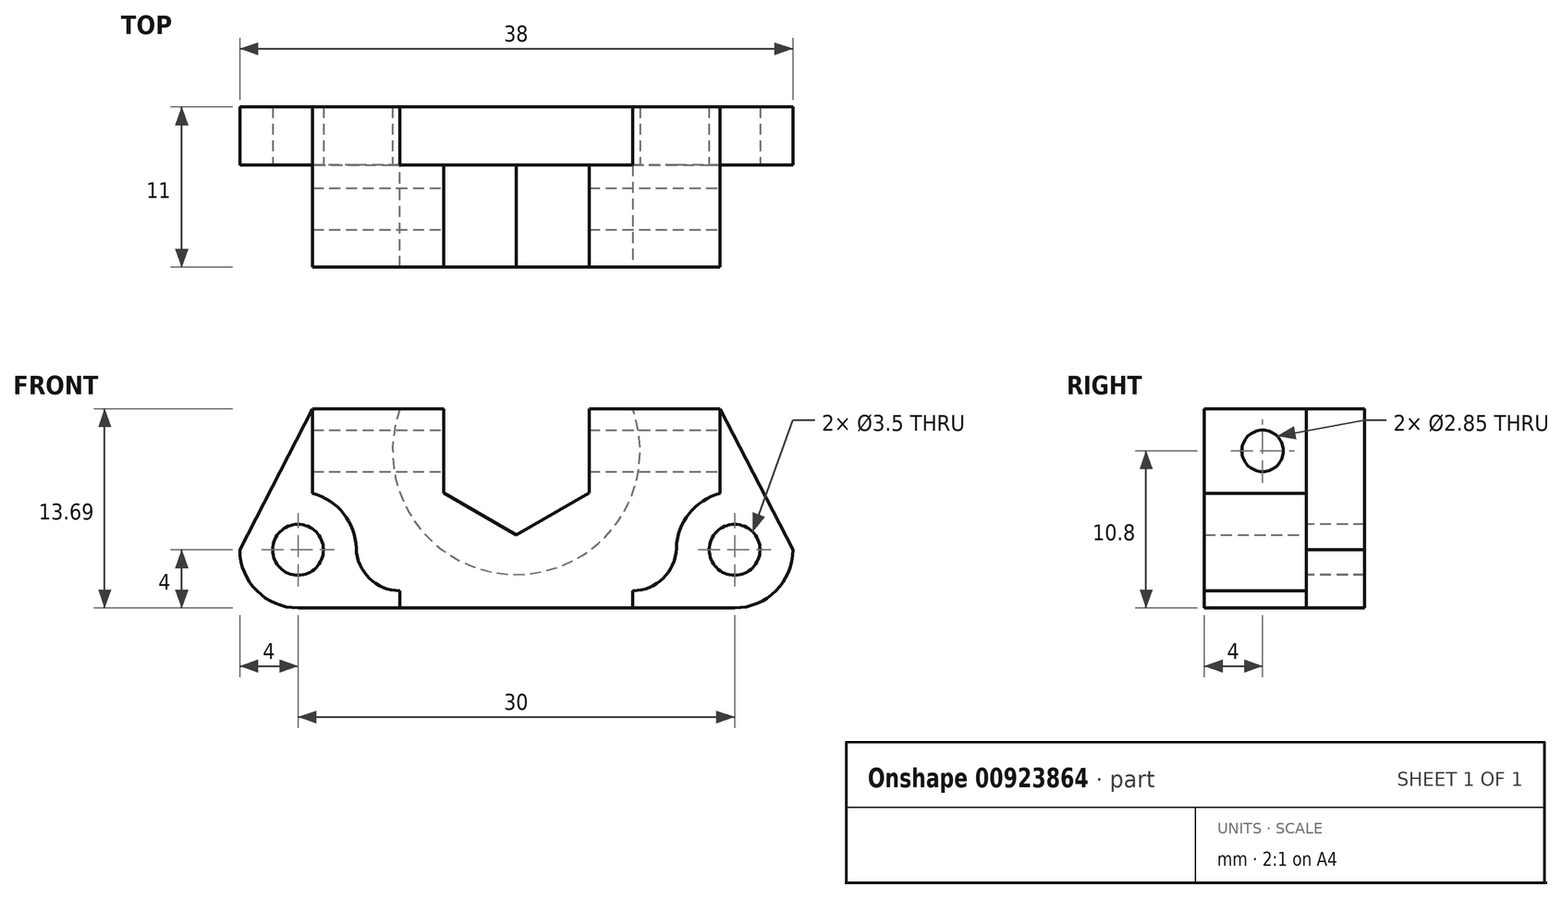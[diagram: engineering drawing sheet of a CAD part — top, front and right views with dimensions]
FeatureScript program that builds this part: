
annotation { "Feature Type Name" : "Feature", "Feature Type Description" : "" }
export const myFeature = defineFeature(function(context is Context, id is Id, definition is map)
    precondition{}
    {
        {
            var Q0;
            Q0=qCreatedBy(makeId("Front.planeOp"),FACE);
            var sketch = newSketch(context, id + "F0", { "sketchPlane" : qUnion([Q0])});
            skLineSegment(sketch, "E0.0", {"start": v(5, 2.89) * mm, "end": v(5, -2.89) * mm});
            skLineSegment(sketch, "E0.1", {"start": v(5, -2.89) * mm, "end": v(0, -5.77) * mm});
            skLineSegment(sketch, "E0.2", {"start": v(0, -5.77) * mm, "end": v(-5, -2.89) * mm});
            skLineSegment(sketch, "E0.3", {"start": v(-5, -2.89) * mm, "end": v(-5, 2.89) * mm});
            skPoint(sketch, "E0.0.midPoint", {"position": v(5, 0) * mm});
            skLineSegment(sketch, "E1", {"start": v(5, 2.89) * mm, "end": v(14, 2.89) * mm});
            skLineSegment(sketch, "E2", {"start": v(-5, 2.89) * mm, "end": v(-14, 2.89) * mm});
            skLineSegment(sketch, "E3.bottom", {"start": v(-14, 2.89) * mm, "end": v(-5, 2.89) * mm});
            skLineSegment(sketch, "E3.top", {"start": v(-14, -9.61) * mm, "end": v(14, -9.61) * mm});
            skLineSegment(sketch, "E3.left", {"start": v(-14, 2.89) * mm, "end": v(-14, -9.61) * mm});
            skLineSegment(sketch, "E3.right", {"start": v(14, 2.89) * mm, "end": v(14, -9.61) * mm});
            skSolve(sketch);
        }
        {
            var Q0;
            Q0 = qSketchRegion(id + "F0", true);
            extrude(context, id + "F1", {"entities" : qUnion([Q0]), "depth" : 7 * mm, "offsetDistance" : 25 * mm});
        }
        {
            var Q0;
            Q0=makeQuery(id+"F1.opExtrude","SWEPT_FACE",FACE,{"disambiguationData":[OSD([sQuery(id+"F0.wireOp",EDGE,"E3.right")])]});
            var sketch = newSketch(context, id + "F2", { "sketchPlane" : qUnion([Q0])});
            skLineSegment(sketch, "E4", {"start": v(0, 0) * mm, "end": v(-6, 0) * mm});
            skCircle(sketch, "E5", {"center": v(-3, 0) * mm, "radius": 1.43 * mm});
            skSolve(sketch);
        }
        {
            var Q0;
            Q0 = qSketchRegion(id + "F2", true);
            extrude(context, id + "F3", {"entities" : qUnion([Q0]), "operationType" : NewBodyOperationType.REMOVE, "oppositeDirection" : true, "depth" : 34.2 * mm, "offsetDistance" : 25 * mm});
        }
        {
            var Q0;
            Q0=makeQuery(id+"F1.opExtrude","CAP_FACE",FACE,{"disambiguationData":[OSD([sQuery(id+"F0.wireOp",EDGE,"E0.0"),sQuery(id+"F0.wireOp",EDGE,"E0.1"),sQuery(id+"F0.wireOp",EDGE,"E0.2"),sQuery(id+"F0.wireOp",EDGE,"E0.3"),sQuery(id+"F0.wireOp",EDGE,"E1"),sQuery(id+"F0.wireOp",EDGE,"E2"),sQuery(id+"F0.wireOp",EDGE,"E3.top"),sQuery(id+"F0.wireOp",EDGE,"E3.left"),sQuery(id+"F0.wireOp",EDGE,"E3.right")])],"isStart":true});
            var sketch = newSketch(context, id + "F4", { "sketchPlane" : qUnion([Q0])});
            skArc(sketch, "E6", {"start": v(-8, 2.89) * mm, "mid": v(0, -8.5) * mm, "end": v(8, 2.89) * mm});
            skLineSegment(sketch, "E7", {"start": v(0, 0) * mm, "end": v(0, -6.8) * mm});
            skLineSegment(sketch, "E8", {"start": v(0, -6.8) * mm, "end": v(-15, -6.8) * mm});
            skCircle(sketch, "E9", {"center": v(-15, -6.8) * mm, "radius": 1.75 * mm});
            skCircle(sketch, "E10.MirrorC", {"center": v(15, -6.8) * mm, "radius": 1.75 * mm});
            skLineSegment(sketch, "E11.0", {"start": v(8, 2.89) * mm, "end": v(14, 2.89) * mm});
            skLineSegment(sketch, "E12.0", {"start": v(-8, 2.89) * mm, "end": v(-14, 2.89) * mm});
            skArc(sketch, "E13", {"start": v(-19, -6.8) * mm, "mid": v(-17.83, -9.63) * mm, "end": v(-15, -10.8) * mm});
            skArc(sketch, "E14", {"start": v(15, -10.8) * mm, "mid": v(17.83, -9.63) * mm, "end": v(19, -6.8) * mm});
            skLineSegment(sketch, "E15", {"start": v(-14, 2.89) * mm, "end": v(-19, -6.8) * mm});
            skLineSegment(sketch, "E16.MirrorCS", {"start": v(14, 2.89) * mm, "end": v(19, -6.8) * mm});
            skLineSegment(sketch, "E17", {"start": v(15, -10.8) * mm, "end": v(-15, -10.8) * mm});
            skPoint(sketch, "E18.orphan", {"position": v(5, 2.89) * mm});
            skPoint(sketch, "E19.orphan", {"position": v(-5, 2.89) * mm});
            skSolve(sketch);
        }
        {
            var Q0;
            Q0 = qSketchRegion(id + "F4", true);
            extrude(context, id + "F5", {"entities" : qUnion([Q0]), "operationType" : NewBodyOperationType.ADD, "depth" : 4 * mm, "offsetDistance" : 25 * mm});
        }
        {
            var Q0;
            Q0=makeQuery(id+"F5.opExtrude","CAP_FACE",FACE,{"disambiguationData":[OSD([sQuery(id+"F4.wireOp",EDGE,"E6"),sQuery(id+"F4.wireOp",EDGE,"E9"),sQuery(id+"F4.wireOp",EDGE,"E10.MirrorC"),sQuery(id+"F4.wireOp",EDGE,"E11.0"),sQuery(id+"F4.wireOp",EDGE,"E12.0"),sQuery(id+"F4.wireOp",EDGE,"E13"),sQuery(id+"F4.wireOp",EDGE,"E14"),sQuery(id+"F4.wireOp",EDGE,"E15"),sQuery(id+"F4.wireOp",EDGE,"E16.MirrorCS"),sQuery(id+"F4.wireOp",EDGE,"E17")])],"isStart":true});
            var sketch = newSketch(context, id + "F6", { "sketchPlane" : qUnion([Q0])});
            skCircle(sketch, "E20", {"center": v(-15, -6.8) * mm, "radius": 4 * mm});
            skCircle(sketch, "E21", {"center": v(15, -6.8) * mm, "radius": 4 * mm});
            skSolve(sketch);
        }
        {
            var Q0;
            Q0 = qSketchRegion(id + "F6", true);
            extrude(context, id + "F7", {"entities" : qUnion([Q0]), "operationType" : NewBodyOperationType.REMOVE, "depth" : 25 * mm, "offsetDistance" : 25 * mm});
        }
        {
            var Q0;
            Q0=makeQuery(id+"F7.boolean.opBoolean","INTERSECT",EDGE,{"derivedFrom":[makeQuery(id+"F1.opExtrude","SWEPT_FACE",FACE,{"disambiguationData":[OSD([sQuery(id+"F0.wireOp",EDGE,"E3.top")])]}),makeQuery(id+"F7.opExtrude","SWEPT_FACE",FACE,{"disambiguationData":[OSD([sQuery(id+"F6.wireOp",EDGE,"E20")])]})]});
            var Q1;
            Q1=makeQuery(id+"F7.boolean.opBoolean","INTERSECT",EDGE,{"derivedFrom":[makeQuery(id+"F1.opExtrude","SWEPT_FACE",FACE,{"disambiguationData":[OSD([sQuery(id+"F0.wireOp",EDGE,"E3.top")])]}),makeQuery(id+"F7.opExtrude","SWEPT_FACE",FACE,{"disambiguationData":[OSD([sQuery(id+"F6.wireOp",EDGE,"E21")])]})]});
            fillet(context, id + "F8", {"entities" : qUnion([Q0, Q1]), "tangentPropagation" : true, "radius" : 3 * mm, "defaultsChanged" : false, "vertexSettings" : [], "allowEdgeOverflow" : false});
        }
        {
            var Q0;
            Q0=makeQuery(id+"F1.opExtrude","SWEPT_FACE",FACE,{"disambiguationData":[OSD([sQuery(id+"F0.wireOp",EDGE,"E3.top")])]});
            var Q1;
            Q1=makeQuery(id+"F5.opExtrude","SWEPT_FACE",FACE,{"disambiguationData":[OSD([sQuery(id+"F4.wireOp",EDGE,"E17")])]});
            extrude(context, id + "F9", {"entities" : qUnion([Q0]), "operationType" : NewBodyOperationType.ADD, "endBound" : BoundingType.UP_TO_SURFACE, "depth" : 25 * mm, "endBoundEntityFace" : qUnion([Q1]), "offsetDistance" : 25 * mm});
        }
    });
